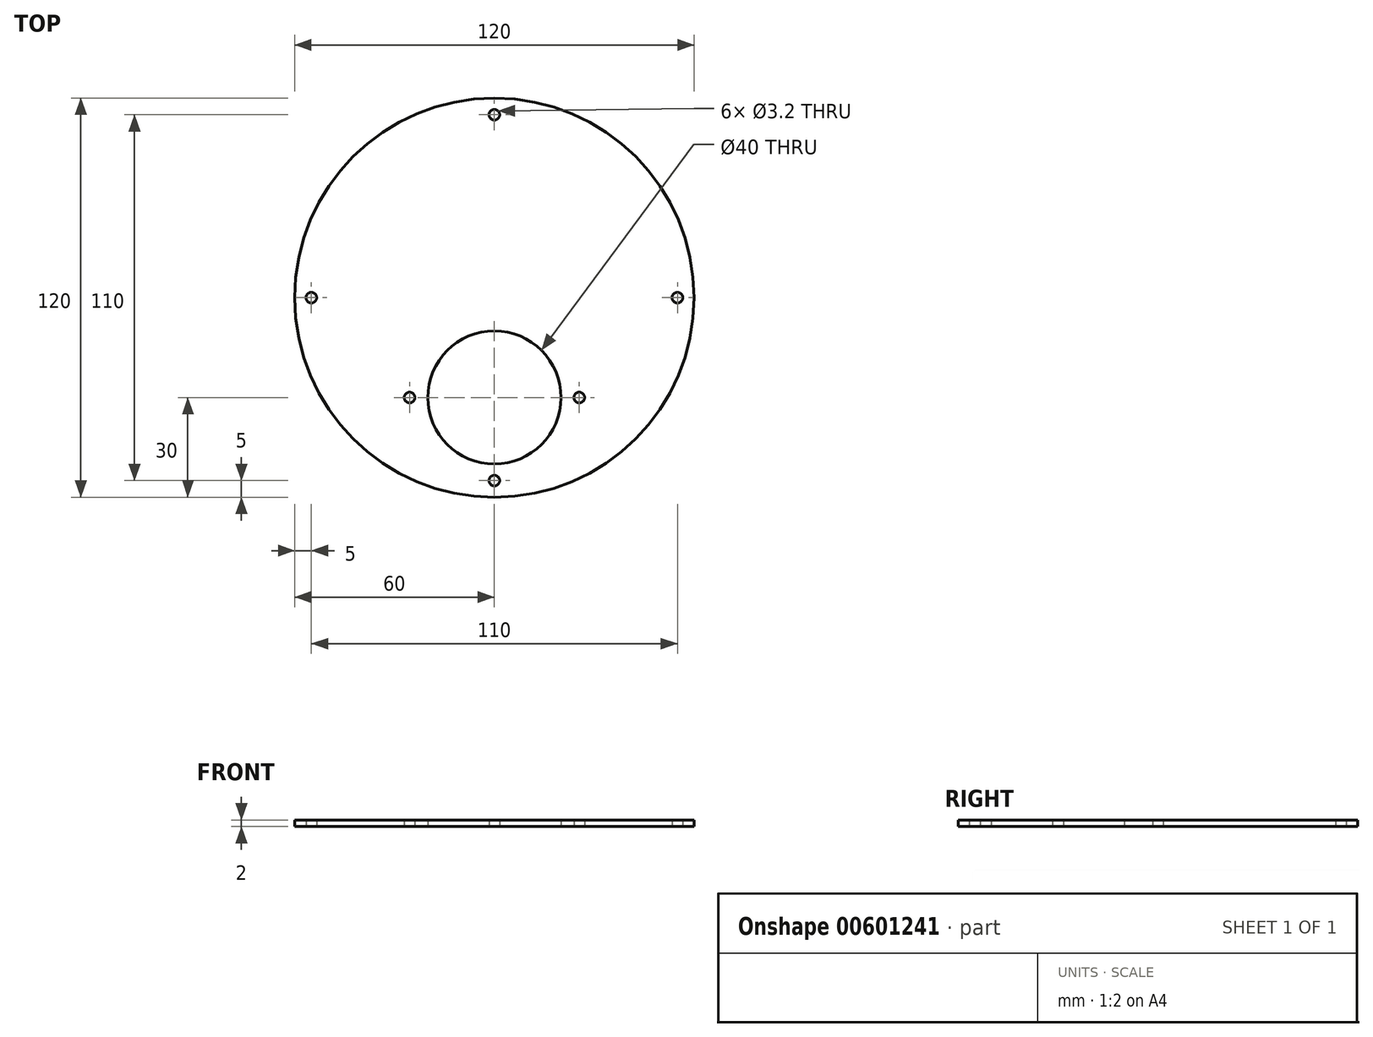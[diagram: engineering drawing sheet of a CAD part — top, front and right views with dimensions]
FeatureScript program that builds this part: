
annotation { "Feature Type Name" : "Feature", "Feature Type Description" : "" }
export const myFeature = defineFeature(function(context is Context, id is Id, definition is map)
    precondition{}
    {
        {
            var Q0;
            Q0=qCreatedBy(makeId("Top.planeOp"),FACE);
            var sketch = newSketch(context, id + "F0", { "sketchPlane" : qUnion([Q0])});
            skCircle(sketch, "E0", {"center": v(0, 0) * mm, "radius": 60 * mm});
            skCircle(sketch, "E1", {"center": v(0, -30) * mm, "radius": 20 * mm});
            skCircle(sketch, "E2", {"center": v(-25.5, -30) * mm, "radius": 1.6 * mm});
            skCircle(sketch, "E3", {"center": v(25.5, -30) * mm, "radius": 1.6 * mm});
            skCircle(sketch, "E4", {"center": v(55, 0) * mm, "radius": 1.6 * mm});
            skCircle(sketch, "E5.1.0", {"center": v(0, 55) * mm, "radius": 1.6 * mm});
            skCircle(sketch, "E5.2.0", {"center": v(-55, 0) * mm, "radius": 1.6 * mm});
            skCircle(sketch, "E5.3.0", {"center": v(0, -55) * mm, "radius": 1.6 * mm});
            skSolve(sketch);
        }
        {
            var Q0;
            Q0=makeQuery(id+"F0.imprint","IMPRINT",FACE,{"disambiguationData":[TD([[makeQuery(id+"F0.imprint","IMPRINT",EDGE,{"derivedFrom":sQuery(id+"F0.wireOp",EDGE,"E0")}),1.0]])]});
            extrude(context, id + "F1", {"entities" : qUnion([Q0]), "depth" : 2 * mm, "offsetDistance" : 25 * mm});
        }
    });
